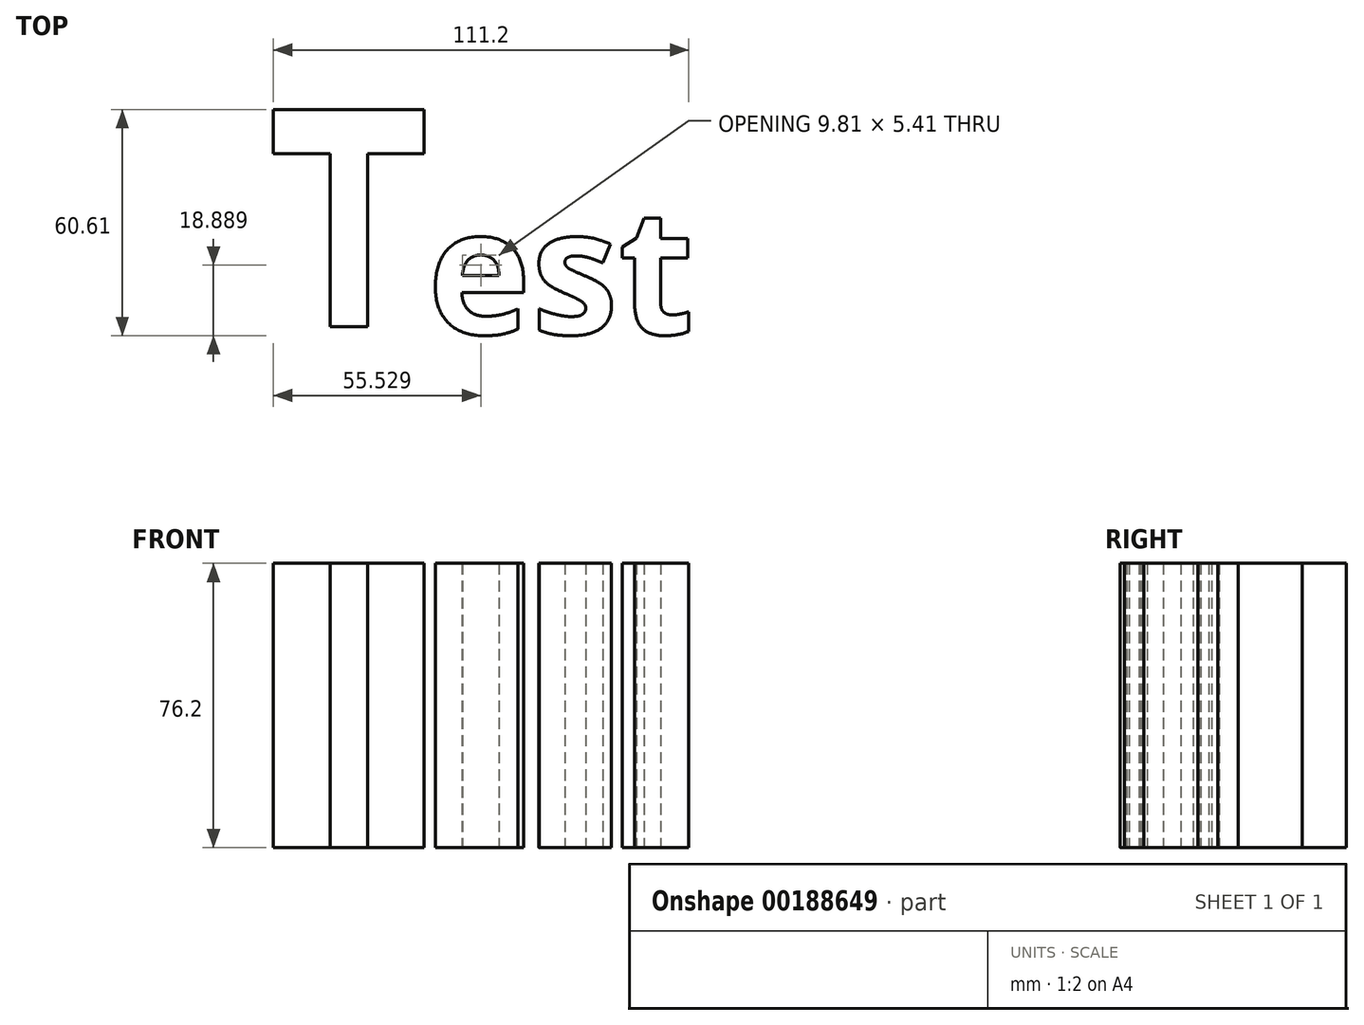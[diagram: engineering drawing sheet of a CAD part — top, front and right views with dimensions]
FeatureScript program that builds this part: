
annotation { "Feature Type Name" : "Feature", "Feature Type Description" : "" }
export const myFeature = defineFeature(function(context is Context, id is Id, definition is map)
    precondition{}
    {
        {
            var Q0;
            Q0=qCreatedBy(makeId("Top.planeOp"),FACE);
            var sketch = newSketch(context, id + "F0", { "sketchPlane" : qUnion([Q0])});
            skLineSegment(sketch, "E0", {"start": v(-52.23, 25.13) * mm, "end": v(-52.23, -21.18) * mm});
            skLineSegment(sketch, "E1", {"start": v(-52.23, -21.18) * mm, "end": v(-42.13, -21.18) * mm});
            skLineSegment(sketch, "E2", {"start": v(-42.13, -21.18) * mm, "end": v(-42.13, 25.13) * mm});
            skLineSegment(sketch, "E3", {"start": v(-42.13, 25.13) * mm, "end": v(-26.98, 25.13) * mm});
            skLineSegment(sketch, "E4", {"start": v(-26.98, 25.13) * mm, "end": v(-26.98, 36.99) * mm});
            skLineSegment(sketch, "E5", {"start": v(-26.98, 36.99) * mm, "end": v(-67.39, 36.99) * mm});
            skLineSegment(sketch, "E6", {"start": v(-67.39, 36.99) * mm, "end": v(-67.39, 25.13) * mm});
            skLineSegment(sketch, "E7", {"start": v(-67.39, 25.13) * mm, "end": v(-52.23, 25.13) * mm});
            skText(sketch, "E8", { "text": "est", "fontName": "OpenSans-Bold.ttf"});
            const initialGuessF0  = {"E8": [-0.02612, -0.02316, 1, 0, 0.0338]};
            skSetInitialGuess(sketch, initialGuessF0);
            skSolve(sketch);
        }
        {
            var Q0;
            Q0 = qSketchRegion(id + "F0", true);
            extrude(context, id + "F1", {"entities" : qUnion([Q0]), "depth" : 76.2 * mm});
        }
    });
